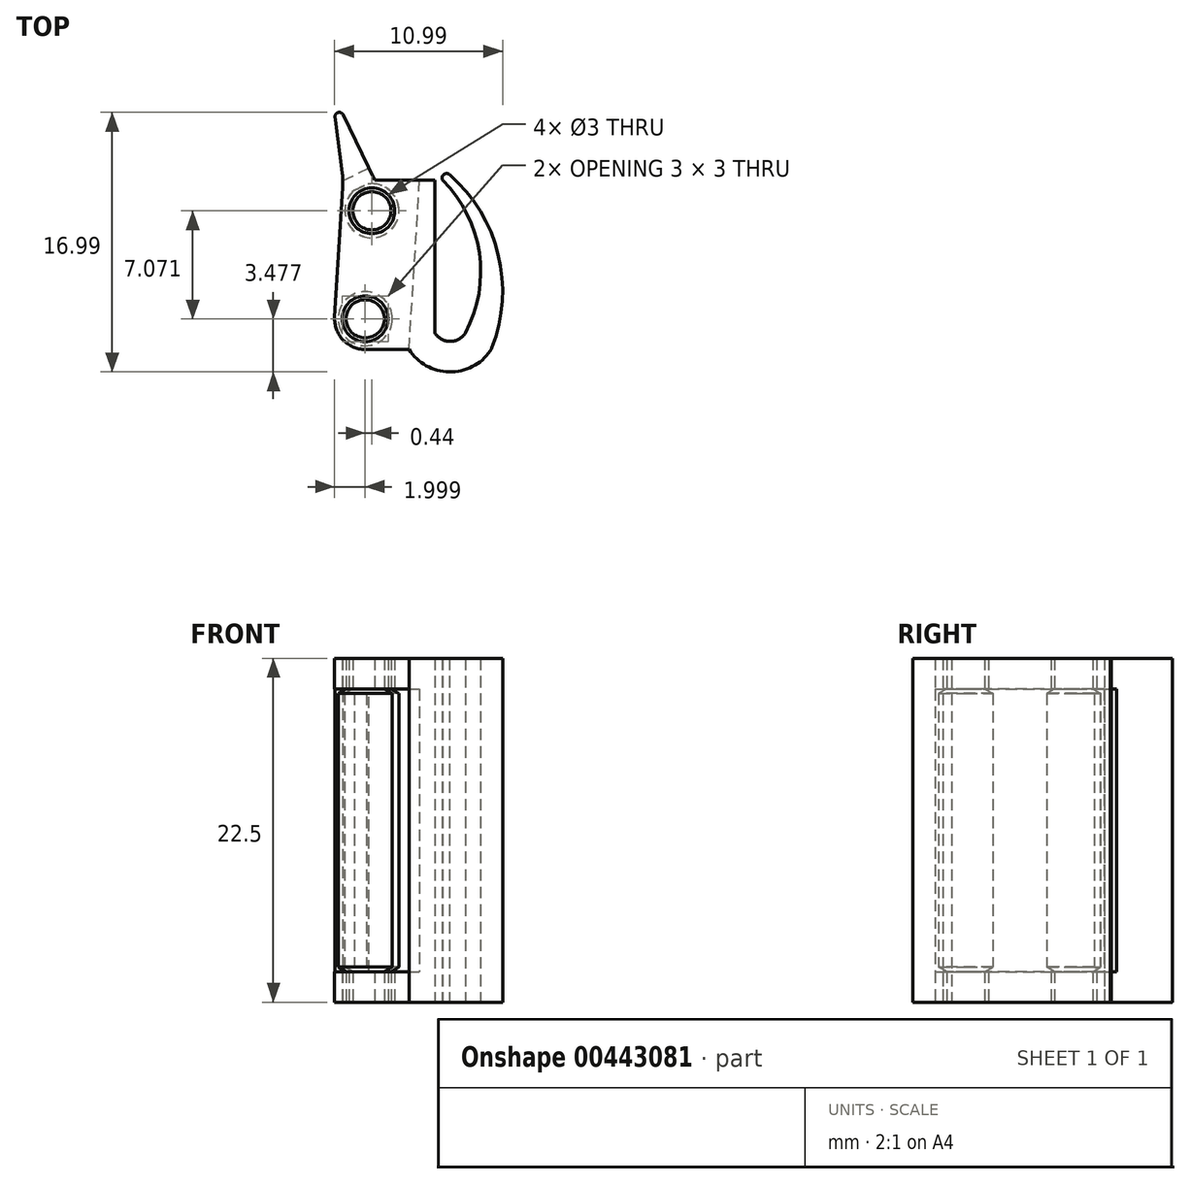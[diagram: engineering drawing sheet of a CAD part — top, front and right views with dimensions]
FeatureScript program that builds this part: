
annotation { "Feature Type Name" : "Feature", "Feature Type Description" : "" }
export const myFeature = defineFeature(function(context is Context, id is Id, definition is map)
    precondition{}
    {
        {
            var Q0;
            Q0=qCreatedBy(makeId("Top.planeOp"),FACE);
            var sketch = newSketch(context, id + "F0", { "sketchPlane" : qUnion([Q0])});
            skLineSegment(sketch, "E0", {"start": v(-4.57, 11) * mm, "end": v(-4.57, 1) * mm});
            skLineSegment(sketch, "E1", {"start": v(-4.57, 1) * mm, "end": v(-2.57, 1) * mm, "construction": true});
            skArc(sketch, "E2", {"start": v(-2.57, 1) * mm, "mid": v(-1.66, 6.26) * mm, "end": v(-4.07, 11) * mm});
            skArc(sketch, "E3", {"start": v(-4.57, 1) * mm, "mid": v(-3.57, 0.46) * mm, "end": v(-2.57, 1) * mm});
            skArc(sketch, "E4.0", {"start": v(-6.26, -0.06) * mm, "mid": v(-3.63, -1.54) * mm, "end": v(-0.95, -0.16) * mm});
            skLineSegment(sketch, "E5", {"start": v(-4.07, 11) * mm, "end": v(-3.61, 11.38) * mm, "construction": true});
            skArc(sketch, "E6", {"start": v(-0.84, 0.04) * mm, "mid": v(-0.43, 6.15) * mm, "end": v(-3.61, 11.38) * mm});
            skArc(sketch, "E7", {"start": v(-3.61, 11.38) * mm, "mid": v(-4, 11.38) * mm, "end": v(-4.07, 11) * mm});
            skLineSegment(sketch, "E8", {"start": v(-4.57, 11) * mm, "end": v(-5.57, 11) * mm});
            skLineSegment(sketch, "E9", {"start": v(-5.57, 11) * mm, "end": v(-6.26, -0.06) * mm});
            skLineSegment(sketch, "E10", {"start": v(-6.26, -0.06) * mm, "end": v(-9.13, -0.06) * mm});
            skLineSegment(sketch, "E11", {"start": v(-5.57, 11) * mm, "end": v(-10.57, 11) * mm});
            skLineSegment(sketch, "E12", {"start": v(-10.6, 10.54) * mm, "end": v(-11.13, 2.06) * mm});
            skPoint(sketch, "E13", {"position": v(-9.13, 1.94) * mm});
            skPoint(sketch, "E14", {"position": v(-8.7, 9) * mm});
            skCircle(sketch, "E15", {"center": v(-9.13, 1.94) * mm, "radius": 1.5 * mm});
            skCircle(sketch, "E16", {"center": v(-9.13, 1.94) * mm, "radius": 1.25 * mm});
            skCircle(sketch, "E17", {"center": v(-8.7, 9) * mm, "radius": 1.5 * mm});
            skCircle(sketch, "E18", {"center": v(-8.7, 9) * mm, "radius": 1.25 * mm});
            skPoint(sketch, "E19.visualSharp", {"position": v(-11.26, -0.06) * mm});
            skArc(sketch, "E19.filletArc", {"start": v(-11.13, 2.06) * mm, "mid": v(-10.59, 0.57) * mm, "end": v(-9.13, -0.06) * mm});
            skLineSegment(sketch, "E20", {"start": v(-8.5, 11) * mm, "end": v(-10.57, 15.29) * mm});
            skLineSegment(sketch, "E21", {"start": v(-10.57, 15.29) * mm, "end": v(-11.08, 15.04) * mm, "construction": true});
            skLineSegment(sketch, "E22", {"start": v(-11.07, 14.94) * mm, "end": v(-10.63, 11.48) * mm});
            skArc(sketch, "E23", {"start": v(-10.57, 15.29) * mm, "mid": v(-10.93, 15.43) * mm, "end": v(-11.1, 15.09) * mm});
            skPoint(sketch, "E24.visualSharp", {"position": v(-11.08, 15.04) * mm});
            skArc(sketch, "E24.filletArc", {"start": v(-11.07, 14.94) * mm, "mid": v(-11.08, 15.01) * mm, "end": v(-11.1, 15.09) * mm});
            skPoint(sketch, "E25.visualSharp", {"position": v(-10.57, 11) * mm});
            skArc(sketch, "E25.filletArc", {"start": v(-10.6, 10.54) * mm, "mid": v(-10.6, 11) * mm, "end": v(-10.63, 11.48) * mm});
            skPoint(sketch, "E26.visualSharp", {"position": v(-0.88, -0.06) * mm});
            skArc(sketch, "E26.filletArc", {"start": v(-0.95, -0.16) * mm, "mid": v(-0.89, -0.07) * mm, "end": v(-0.84, 0.04) * mm});
            skLineSegment(sketch, "E27", {"start": v(-10.57, 11) * mm, "end": v(-8.5, 11) * mm});
            skArc(sketch, "E28", {"start": v(-8.5, 11) * mm, "mid": v(-9.57, 10.89) * mm, "end": v(-10.6, 10.54) * mm});
            skSolve(sketch);
        }
        {
            var Q0;
            Q0=makeQuery(id+"F0.imprint","IMPRINT",FACE,{"disambiguationData":[TD([[makeQuery(id+"F0.imprint","IMPRINT",EDGE,{"derivedFrom":sQuery(id+"F0.wireOp",EDGE,"E9")}),-1.0]])]});
            extrude(context, id + "F1", {"entities" : qUnion([Q0]), "depth" : 22.5 * mm});
        }
        {
            var Q0;
            Q0=makeQuery(id+"F1.opExtrude","SWEPT_FACE",FACE,{"disambiguationData":[OSD([sQuery(id+"F0.wireOp",EDGE,"E12")])]});
            var sketch = newSketch(context, id + "F2", { "sketchPlane" : qUnion([Q0])});
            skLineSegment(sketch, "E29.bottom", {"start": v(-11.42, 2) * mm, "end": v(2.67, 2) * mm});
            skLineSegment(sketch, "E29.top", {"start": v(-11.42, 20.5) * mm, "end": v(2.67, 20.5) * mm});
            skLineSegment(sketch, "E29.left", {"start": v(-11.42, 2) * mm, "end": v(-11.42, 20.5) * mm});
            skLineSegment(sketch, "E29.right", {"start": v(2.67, 2) * mm, "end": v(2.67, 20.5) * mm});
            skSolve(sketch);
        }
        {
            var Q0;
            {var subQ0=sQuery(id+"F2.wireOp",EDGE,"E29.bottom");var subQ3=sQuery(id+"F0.wireOp",EDGE,"E12");var subQ6=makeQuery(id+"F1.opExtrude","SWEPT_EDGE",EDGE,{"disambiguationData":[OSD([subQ3,sQuery(id+"F0.wireOp",EDGE,"E19.filletArc")])]});var subQ7=makeQuery(id+"F2.imprint","INTERSECT",VERTEX,{"derivedFrom":[subQ6,subQ0]});Q0=makeQuery(id+"F2.imprint","IMPRINT",FACE,{"disambiguationData":[TD([[makeQuery(id+"F2.imprint","IMPRINT",EDGE,{"disambiguationData":[TD([[subQ7,1.0]])],"derivedFrom":subQ6}),-1.0]])]});}
            var Q1;
            {var subQ0=sQuery(id+"F2.wireOp",EDGE,"E29.right");Q1=makeQuery(id+"F2.imprint","IMPRINT",FACE,{"disambiguationData":[TD([[makeQuery(id+"F2.imprint","IMPRINT",EDGE,{"derivedFrom":subQ0}),1.0]])]});}
            var Q2;
            {var subQ0=sQuery(id+"F2.wireOp",EDGE,"E29.left");Q2=makeQuery(id+"F2.imprint","IMPRINT",FACE,{"disambiguationData":[TD([[makeQuery(id+"F2.imprint","IMPRINT",EDGE,{"derivedFrom":subQ0}),-1.0]])]});}
            extrude(context, id + "F3", {"entities" : qUnion([Q0, Q1, Q2]), "operationType" : NewBodyOperationType.REMOVE, "oppositeDirection" : true, "depth" : 25 * mm});
        }
        {
            var Q0;
            Q0=makeQuery(id+"F0.imprint","IMPRINT",FACE,{"disambiguationData":[TD([[makeQuery(id+"F0.imprint","IMPRINT",EDGE,{"derivedFrom":sQuery(id+"F0.wireOp",EDGE,"E20")}),1.0]])]});
            var Q1;
            Q1=makeQuery(id+"F0.imprint","IMPRINT",FACE,{"disambiguationData":[TD([[makeQuery(id+"F0.imprint","IMPRINT",EDGE,{"derivedFrom":sQuery(id+"F0.wireOp",EDGE,"E0")}),-1.0]])]});
            extrude(context, id + "F4", {"entities" : qUnion([Q0, Q1]), "operationType" : NewBodyOperationType.ADD, "depth" : 22.5 * mm});
        }
        {
            var Q0;
            Q0=makeQuery(id+"F0.imprint","IMPRINT",FACE,{"disambiguationData":[TD([[makeQuery(id+"F0.imprint","IMPRINT",EDGE,{"derivedFrom":sQuery(id+"F0.wireOp",EDGE,"E18")}),1.0]])]});
            var Q1;
            Q1=makeQuery(id+"F0.imprint","IMPRINT",FACE,{"disambiguationData":[TD([[makeQuery(id+"F0.imprint","IMPRINT",EDGE,{"derivedFrom":sQuery(id+"F0.wireOp",EDGE,"E16")}),1.0]])]});
            extrude(context, id + "F5", {"entities" : qUnion([Q0, Q1]), "depth" : 2 * mm});
        }
        {
            var Q0;
            Q0=makeQuery(id+"F5.opExtrude","CAP_FACE",FACE,{"disambiguationData":[OSD([sQuery(id+"F0.wireOp",EDGE,"E18")])],"isStart":false});
            var Q1;
            Q1=makeQuery(id+"F5.opExtrude","CAP_FACE",FACE,{"disambiguationData":[OSD([sQuery(id+"F0.wireOp",EDGE,"E16")])],"isStart":false});
            extrude(context, id + "F6", {"entities" : qUnion([Q0, Q1]), "depth" : 0.3 * mm, "hasDraft" : true, "draftAngle" : 60 * degree});
        }
        {
            var Q0;
            Q0=makeQuery(id+"F6.opExtrude","CAP_FACE",FACE,{"disambiguationData":[OSD([sQuery(id+"F0.wireOp",EDGE,"E18")])],"isStart":false});
            var Q1;
            Q1=makeQuery(id+"F6.opExtrude","CAP_FACE",FACE,{"disambiguationData":[OSD([sQuery(id+"F0.wireOp",EDGE,"E16")])],"isStart":false});
            extrude(context, id + "F7", {"entities" : qUnion([Q0, Q1]), "depth" : 17.9 * mm});
        }
        {
            var Q0;
            Q0=makeQuery(id+"F7.opExtrude","CAP_FACE",FACE,{"disambiguationData":[OSD([sQuery(id+"F0.wireOp",EDGE,"E18")])],"isStart":false});
            var Q1;
            Q1=makeQuery(id+"F7.opExtrude","CAP_FACE",FACE,{"disambiguationData":[OSD([sQuery(id+"F0.wireOp",EDGE,"E16")])],"isStart":false});
            extrude(context, id + "F8", {"entities" : qUnion([Q0, Q1]), "depth" : 0.3 * mm, "hasDraft" : true, "draftAngle" : 60 * degree, "draftPullDirection" : true});
        }
        {
            var Q0;
            Q0=makeQuery(id+"F8.opExtrude","CAP_FACE",FACE,{"disambiguationData":[OSD([sQuery(id+"F0.wireOp",EDGE,"E18")])],"isStart":false});
            var Q1;
            Q1=makeQuery(id+"F8.opExtrude","CAP_FACE",FACE,{"disambiguationData":[OSD([sQuery(id+"F0.wireOp",EDGE,"E16")])],"isStart":false});
            extrude(context, id + "F9", {"entities" : qUnion([Q0, Q1]), "depth" : 2 * mm});
        }
        {
            var Q0;
            Q0=makeQuery(id+"F4.opExtrude","SWEPT_FACE",FACE,{"disambiguationData":[OSD([sQuery(id+"F0.wireOp",EDGE,"E20")])]});
            var sketch = newSketch(context, id + "F10", { "sketchPlane" : qUnion([Q0])});
            skLineSegment(sketch, "E30.bottom", {"start": v(13.61, 2) * mm, "end": v(14.5, 2) * mm});
            skLineSegment(sketch, "E30.top", {"start": v(13.61, 20.5) * mm, "end": v(14.5, 20.5) * mm});
            skLineSegment(sketch, "E30.left", {"start": v(13.61, 2) * mm, "end": v(13.61, 20.5) * mm});
            skLineSegment(sketch, "E30.right", {"start": v(14.5, 2) * mm, "end": v(14.5, 20.5) * mm});
            skSolve(sketch);
        }
        {
            var Q0;
            Q0=makeQuery(id+"F10.imprint","IMPRINT",FACE,{"disambiguationData":[TD([[makeQuery(id+"F10.imprint","IMPRINT",EDGE,{"derivedFrom":sQuery(id+"F10.wireOp",EDGE,"E30.bottom")}),1.0]])]});
            extrude(context, id + "F11", {"entities" : qUnion([Q0]), "operationType" : NewBodyOperationType.REMOVE, "oppositeDirection" : true, "depth" : 25 * mm});
        }
    });
